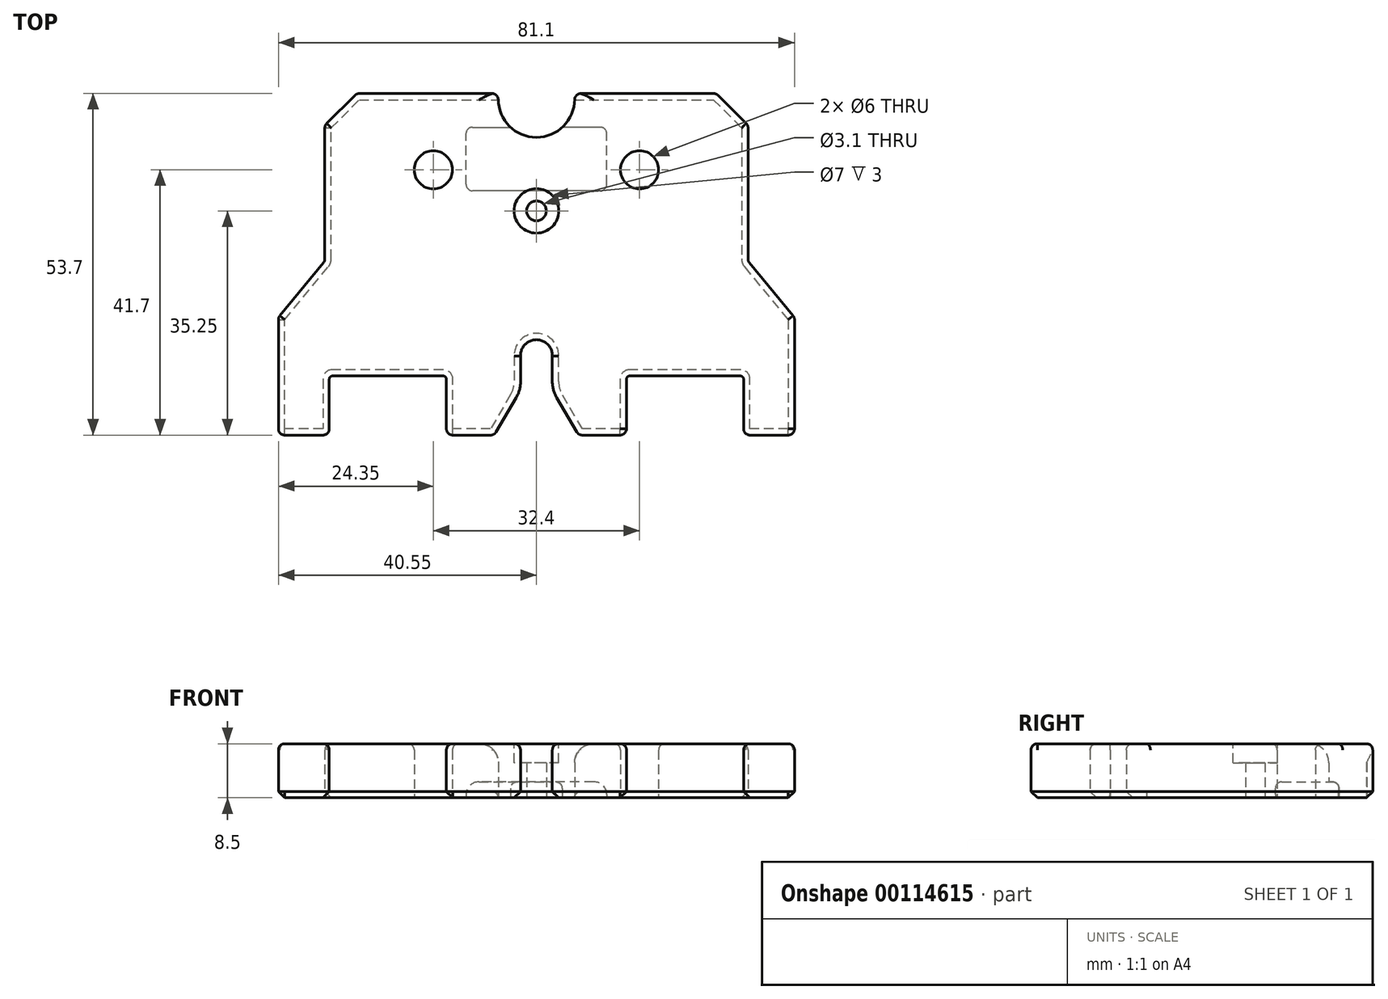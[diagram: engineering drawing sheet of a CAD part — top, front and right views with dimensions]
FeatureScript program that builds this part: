
annotation { "Feature Type Name" : "Feature", "Feature Type Description" : "" }
export const myFeature = defineFeature(function(context is Context, id is Id, definition is map)
    precondition{}
    {
        {
            var Q0;
            Q0=qCreatedBy(makeId("Top.planeOp"),FACE);
            var sketch = newSketch(context, id + "F0", { "sketchPlane" : qUnion([Q0])});
            skLineSegment(sketch, "E0.bottom", {"start": v(7.21, 0) * mm, "end": v(13.15, 0) * mm});
            skLineSegment(sketch, "E0.top", {"start": v(7, 53.7) * mm, "end": v(27.84, 53.7) * mm});
            skLineSegment(sketch, "E0.right", {"start": v(40.55, 1) * mm, "end": v(40.55, 18.14) * mm});
            skCircle(sketch, "E1", {"center": v(40.55, 0) * mm, "radius": 8 * mm, "construction": true});
            skLineSegment(sketch, "E2", {"start": v(32.55, 1) * mm, "end": v(32.55, 8.8) * mm});
            skLineSegment(sketch, "E3", {"start": v(32.05, 9.3) * mm, "end": v(14.65, 9.3) * mm});
            skLineSegment(sketch, "E4", {"start": v(14.15, 8.8) * mm, "end": v(14.15, 1) * mm});
            skCircle(sketch, "E5", {"center": v(14.14, 0) * mm, "radius": 7.5 * mm, "construction": true});
            skArc(sketch, "E6", {"start": v(2.5, 12.43) * mm, "mid": v(1.8, 14.24) * mm, "end": v(0, 15) * mm});
            skLineSegment(sketch, "E7", {"start": v(2.5, 12.43) * mm, "end": v(2.5, 8.4) * mm});
            skLineSegment(sketch, "E8.trimOffspring", {"start": v(33.55, 0) * mm, "end": v(39.55, 0) * mm});
            skLineSegment(sketch, "E9.trimOffspring", {"start": v(0, 15) * mm, "end": v(0, 46.8) * mm, "construction": true});
            skPoint(sketch, "E0.left.start.orphan", {"position": v(0, 0) * mm});
            skLineSegment(sketch, "E10", {"start": v(6, 52.8) * mm, "end": v(6, 52.7) * mm});
            skArc(sketch, "E11.trimOffspring", {"start": v(0, 46.8) * mm, "mid": v(4.24, 48.56) * mm, "end": v(6, 52.8) * mm});
            skCircle(sketch, "E12", {"center": v(40.55, 0) * mm, "radius": 18.5 * mm, "construction": true});
            skCircle(sketch, "E13", {"center": v(40.55, 18.5) * mm, "radius": 8.85 * mm, "construction": true});
            skLineSegment(sketch, "E14", {"start": v(28.54, 53.4) * mm, "end": v(32.96, 49) * mm});
            skLineSegment(sketch, "E15", {"start": v(33.25, 48.29) * mm, "end": v(33.25, 27.7) * mm});
            skLineSegment(sketch, "E16", {"start": v(40.32, 18.78) * mm, "end": v(33.48, 27.07) * mm});
            skLineSegment(sketch, "E17", {"start": v(40.55, 27.35) * mm, "end": v(33.25, 27.35) * mm, "construction": true});
            skLineSegment(sketch, "E18", {"start": v(40.55, 27.35) * mm, "end": v(40.55, 18.5) * mm, "construction": true});
            skLineSegment(sketch, "E19", {"start": v(3.2, 5.87) * mm, "end": v(6.35, 0.5) * mm});
            skCircle(sketch, "E20", {"center": v(16.2, 41.7) * mm, "radius": 3 * mm});
            skCircle(sketch, "E21", {"center": v(0, 35.25) * mm, "radius": 1.55 * mm});
            skLineSegment(sketch, "E22", {"start": v(0, 33.7) * mm, "end": v(-9.13, 33.7) * mm, "construction": true});
            skCircle(sketch, "E23", {"center": v(0, 53.7) * mm, "radius": 11.05 * mm, "construction": true});
            skLineSegment(sketch, "E24", {"start": v(11.05, 53.7) * mm, "end": v(11.05, 38.4) * mm, "construction": true});
            skLineSegment(sketch, "E25", {"start": v(11.05, 38.4) * mm, "end": v(-11.05, 38.4) * mm, "construction": true});
            skLineSegment(sketch, "E26", {"start": v(-11.05, 53.54) * mm, "end": v(-11.05, 38.4) * mm, "construction": true});
            skLineSegment(sketch, "E27", {"start": v(0, 36.8) * mm, "end": v(-9.83, 36.8) * mm, "construction": true});
            skCircle(sketch, "E28", {"center": v(11.05, 38.4) * mm, "radius": 10 * mm, "construction": true});
            skLineSegment(sketch, "E29", {"start": v(11.05, 48.4) * mm, "end": v(-11.05, 48.4) * mm, "construction": true});
            skPoint(sketch, "E30.visualSharp", {"position": v(2.5, 7.04) * mm});
            skArc(sketch, "E30.filletArc", {"start": v(2.5, 8.4) * mm, "mid": v(2.67, 7.09) * mm, "end": v(3.2, 5.87) * mm});
            skPoint(sketch, "E31.visualSharp", {"position": v(6.64, 0) * mm});
            skArc(sketch, "E31.filletArc", {"start": v(6.35, 0.5) * mm, "mid": v(6.72, 0.13) * mm, "end": v(7.21, 0) * mm});
            skPoint(sketch, "E32.newPointB", {"position": v(14.15, 0) * mm});
            skArc(sketch, "E32.filletArc", {"start": v(13.15, 0) * mm, "mid": v(13.86, 0.3) * mm, "end": v(14.15, 1) * mm});
            skPoint(sketch, "E33.visualSharp", {"position": v(14.15, 9.3) * mm});
            skArc(sketch, "E33.filletArc", {"start": v(14.65, 9.3) * mm, "mid": v(14.3, 9.15) * mm, "end": v(14.15, 8.8) * mm});
            skPoint(sketch, "E34.visualSharp", {"position": v(32.55, 9.3) * mm});
            skArc(sketch, "E34.filletArc", {"start": v(32.55, 8.8) * mm, "mid": v(32.4, 9.15) * mm, "end": v(32.05, 9.3) * mm});
            skPoint(sketch, "E35.visualSharp", {"position": v(32.55, 0) * mm});
            skArc(sketch, "E35.filletArc", {"start": v(32.55, 1) * mm, "mid": v(32.84, 0.3) * mm, "end": v(33.55, 0) * mm});
            skArc(sketch, "E36.filletArc", {"start": v(39.55, 0) * mm, "mid": v(40.26, 0.3) * mm, "end": v(40.55, 1) * mm});
            skArc(sketch, "E37.filletArc", {"start": v(40.55, 18.14) * mm, "mid": v(40.5, 18.48) * mm, "end": v(40.32, 18.78) * mm});
            skPoint(sketch, "E38.visualSharp", {"position": v(33.25, 27.35) * mm});
            skArc(sketch, "E38.filletArc", {"start": v(33.25, 27.7) * mm, "mid": v(33.3, 27.37) * mm, "end": v(33.48, 27.07) * mm});
            skPoint(sketch, "E39.visualSharp", {"position": v(33.25, 48.7) * mm});
            skArc(sketch, "E39.filletArc", {"start": v(33.25, 48.29) * mm, "mid": v(33.17, 48.67) * mm, "end": v(32.96, 49) * mm});
            skPoint(sketch, "E40.visualSharp", {"position": v(28.25, 53.7) * mm});
            skArc(sketch, "E40.filletArc", {"start": v(28.54, 53.4) * mm, "mid": v(28.22, 53.62) * mm, "end": v(27.84, 53.7) * mm});
            skPoint(sketch, "E41.visualSharp", {"position": v(6, 53.7) * mm});
            skArc(sketch, "E41.filletArc", {"start": v(7, 53.7) * mm, "mid": v(6.3, 53.4) * mm, "end": v(6, 52.7) * mm});
            skArc(sketch, "E42.MirrorCS", {"start": v(0, 46.8) * mm, "mid": v(-4.24, 48.56) * mm, "end": v(-6, 52.8) * mm});
            skArc(sketch, "E43.MirrorCS", {"start": v(-7, 53.7) * mm, "mid": v(-6.3, 53.4) * mm, "end": v(-6, 52.7) * mm});
            skLineSegment(sketch, "E44.MirrorCS", {"start": v(-6, 52.8) * mm, "end": v(-6, 52.7) * mm});
            skLineSegment(sketch, "E45.MirrorCS", {"start": v(-7, 53.7) * mm, "end": v(-27.84, 53.7) * mm});
            skArc(sketch, "E46.MirrorCS", {"start": v(-28.54, 53.4) * mm, "mid": v(-28.22, 53.62) * mm, "end": v(-27.84, 53.7) * mm});
            skLineSegment(sketch, "E47.MirrorCS", {"start": v(-28.54, 53.4) * mm, "end": v(-32.96, 49) * mm});
            skArc(sketch, "E48.MirrorCS", {"start": v(-33.25, 48.29) * mm, "mid": v(-33.17, 48.67) * mm, "end": v(-32.96, 49) * mm});
            skLineSegment(sketch, "E49.MirrorCS", {"start": v(-33.25, 48.29) * mm, "end": v(-33.25, 27.7) * mm});
            skArc(sketch, "E50.MirrorCS", {"start": v(-33.25, 27.7) * mm, "mid": v(-33.3, 27.37) * mm, "end": v(-33.48, 27.07) * mm});
            skLineSegment(sketch, "E51.MirrorCS", {"start": v(-40.32, 18.78) * mm, "end": v(-33.48, 27.07) * mm});
            skArc(sketch, "E52.MirrorCS", {"start": v(-40.55, 18.14) * mm, "mid": v(-40.5, 18.48) * mm, "end": v(-40.32, 18.78) * mm});
            skLineSegment(sketch, "E53.MirrorCS", {"start": v(-40.55, 1) * mm, "end": v(-40.55, 18.14) * mm});
            skArc(sketch, "E54.MirrorCS", {"start": v(-39.55, 0) * mm, "mid": v(-40.26, 0.3) * mm, "end": v(-40.55, 1) * mm});
            skLineSegment(sketch, "E55.MirrorCS", {"start": v(-33.55, 0) * mm, "end": v(-39.55, 0) * mm});
            skArc(sketch, "E56.MirrorCS", {"start": v(-32.55, 1) * mm, "mid": v(-32.84, 0.3) * mm, "end": v(-33.55, 0) * mm});
            skLineSegment(sketch, "E57.MirrorCS", {"start": v(-32.55, 1) * mm, "end": v(-32.55, 8.8) * mm});
            skArc(sketch, "E58.MirrorCS", {"start": v(-32.55, 8.8) * mm, "mid": v(-32.4, 9.15) * mm, "end": v(-32.05, 9.3) * mm});
            skLineSegment(sketch, "E59.MirrorCS", {"start": v(-32.05, 9.3) * mm, "end": v(-14.65, 9.3) * mm});
            skArc(sketch, "E60.MirrorCS", {"start": v(-14.65, 9.3) * mm, "mid": v(-14.3, 9.15) * mm, "end": v(-14.15, 8.8) * mm});
            skLineSegment(sketch, "E61.MirrorCS", {"start": v(-14.15, 8.8) * mm, "end": v(-14.15, 1) * mm});
            skArc(sketch, "E62.MirrorCS", {"start": v(-13.15, 0) * mm, "mid": v(-13.86, 0.3) * mm, "end": v(-14.15, 1) * mm});
            skLineSegment(sketch, "E63.MirrorCS", {"start": v(-7.21, 0) * mm, "end": v(-13.15, 0) * mm});
            skArc(sketch, "E64.MirrorCS", {"start": v(-6.35, 0.5) * mm, "mid": v(-6.72, 0.13) * mm, "end": v(-7.21, 0) * mm});
            skLineSegment(sketch, "E65.MirrorCS", {"start": v(-3.2, 5.87) * mm, "end": v(-6.35, 0.5) * mm});
            skArc(sketch, "E66.MirrorCS", {"start": v(-2.5, 8.4) * mm, "mid": v(-2.67, 7.09) * mm, "end": v(-3.2, 5.87) * mm});
            skLineSegment(sketch, "E67.MirrorCS", {"start": v(-2.5, 12.43) * mm, "end": v(-2.5, 8.4) * mm});
            skArc(sketch, "E68.MirrorCS", {"start": v(-2.5, 12.43) * mm, "mid": v(-1.8, 14.24) * mm, "end": v(0, 15) * mm});
            skCircle(sketch, "E69.MirrorC", {"center": v(-16.2, 41.7) * mm, "radius": 3 * mm});
            skSolve(sketch);
        }
        {
            var Q0;
            Q0=makeQuery(id+"F0.imprint","IMPRINT",FACE,{"disambiguationData":[TD([[makeQuery(id+"F0.imprint","IMPRINT",EDGE,{"derivedFrom":sQuery(id+"F0.wireOp",EDGE,"E0.bottom")}),1.0]])]});
            extrude(context, id + "F1", {"entities" : qUnion([Q0]), "depth" : 8.5 * mm});
        }
        {
            var Q0;
            Q0=makeQuery(id+"F1.opExtrude","CAP_FACE",FACE,{"disambiguationData":[OSD([sQuery(id+"F0.wireOp",EDGE,"E0.bottom"),sQuery(id+"F0.wireOp",EDGE,"E0.top"),sQuery(id+"F0.wireOp",EDGE,"E0.right"),sQuery(id+"F0.wireOp",EDGE,"E2"),sQuery(id+"F0.wireOp",EDGE,"E3"),sQuery(id+"F0.wireOp",EDGE,"E4"),sQuery(id+"F0.wireOp",EDGE,"E6"),sQuery(id+"F0.wireOp",EDGE,"E7"),sQuery(id+"F0.wireOp",EDGE,"E8.trimOffspring"),sQuery(id+"F0.wireOp",EDGE,"E10"),sQuery(id+"F0.wireOp",EDGE,"E11.trimOffspring"),sQuery(id+"F0.wireOp",EDGE,"E14"),sQuery(id+"F0.wireOp",EDGE,"E15"),sQuery(id+"F0.wireOp",EDGE,"E16"),sQuery(id+"F0.wireOp",EDGE,"E19"),sQuery(id+"F0.wireOp",EDGE,"E20"),sQuery(id+"F0.wireOp",EDGE,"E21"),sQuery(id+"F0.wireOp",EDGE,"E30.filletArc"),sQuery(id+"F0.wireOp",EDGE,"E31.filletArc"),sQuery(id+"F0.wireOp",EDGE,"E32.filletArc"),sQuery(id+"F0.wireOp",EDGE,"E33.filletArc"),sQuery(id+"F0.wireOp",EDGE,"E34.filletArc"),sQuery(id+"F0.wireOp",EDGE,"E35.filletArc"),sQuery(id+"F0.wireOp",EDGE,"E36.filletArc"),sQuery(id+"F0.wireOp",EDGE,"E37.filletArc"),sQuery(id+"F0.wireOp",EDGE,"E38.filletArc"),sQuery(id+"F0.wireOp",EDGE,"E39.filletArc"),sQuery(id+"F0.wireOp",EDGE,"E40.filletArc"),sQuery(id+"F0.wireOp",EDGE,"E41.filletArc"),sQuery(id+"F0.wireOp",EDGE,"E42.MirrorCS"),sQuery(id+"F0.wireOp",EDGE,"E43.MirrorCS"),sQuery(id+"F0.wireOp",EDGE,"E44.MirrorCS"),sQuery(id+"F0.wireOp",EDGE,"E45.MirrorCS"),sQuery(id+"F0.wireOp",EDGE,"E46.MirrorCS"),sQuery(id+"F0.wireOp",EDGE,"E47.MirrorCS"),sQuery(id+"F0.wireOp",EDGE,"E48.MirrorCS"),sQuery(id+"F0.wireOp",EDGE,"E49.MirrorCS"),sQuery(id+"F0.wireOp",EDGE,"E50.MirrorCS"),sQuery(id+"F0.wireOp",EDGE,"E51.MirrorCS"),sQuery(id+"F0.wireOp",EDGE,"E52.MirrorCS"),sQuery(id+"F0.wireOp",EDGE,"E53.MirrorCS"),sQuery(id+"F0.wireOp",EDGE,"E54.MirrorCS"),sQuery(id+"F0.wireOp",EDGE,"E55.MirrorCS"),sQuery(id+"F0.wireOp",EDGE,"E56.MirrorCS"),sQuery(id+"F0.wireOp",EDGE,"E57.MirrorCS"),sQuery(id+"F0.wireOp",EDGE,"E58.MirrorCS"),sQuery(id+"F0.wireOp",EDGE,"E59.MirrorCS"),sQuery(id+"F0.wireOp",EDGE,"E60.MirrorCS"),sQuery(id+"F0.wireOp",EDGE,"E61.MirrorCS"),sQuery(id+"F0.wireOp",EDGE,"E62.MirrorCS"),sQuery(id+"F0.wireOp",EDGE,"E63.MirrorCS"),sQuery(id+"F0.wireOp",EDGE,"E64.MirrorCS"),sQuery(id+"F0.wireOp",EDGE,"E65.MirrorCS"),sQuery(id+"F0.wireOp",EDGE,"E66.MirrorCS"),sQuery(id+"F0.wireOp",EDGE,"E67.MirrorCS"),sQuery(id+"F0.wireOp",EDGE,"E68.MirrorCS"),sQuery(id+"F0.wireOp",EDGE,"E69.MirrorC")])],"isStart":false});
            var sketch = newSketch(context, id + "F2", { "sketchPlane" : qUnion([Q0])});
            skCircle(sketch, "E70", {"center": v(0, 35.25) * mm, "radius": 3.5 * mm});
            skSolve(sketch);
        }
        {
            var Q0;
            Q0=makeQuery(id+"F2.imprint","IMPRINT",FACE,{"disambiguationData":[TD([[makeQuery(id+"F2.imprint","IMPRINT",EDGE,{"derivedFrom":sQuery(id+"F2.wireOp",EDGE,"E70")}),1.0]])]});
            extrude(context, id + "F3", {"entities" : qUnion([Q0]), "operationType" : NewBodyOperationType.REMOVE, "oppositeDirection" : true, "depth" : 3 * mm});
        }
        {
            var Q0;
            Q0=makeQuery(id+"F0.imprint","IMPRINT",FACE,{"disambiguationData":[TD([[makeQuery(id+"F0.imprint","IMPRINT",EDGE,{"derivedFrom":sQuery(id+"F0.wireOp",EDGE,"E0.bottom")}),1.0]])]});
            var sketch = newSketch(context, id + "F4", { "sketchPlane" : qUnion([Q0])});
            skLineSegment(sketch, "E71", {"start": v(0, 54.27) * mm, "end": v(0, 38.4) * mm, "construction": true});
            skLineSegment(sketch, "E72", {"start": v(0, 38.4) * mm, "end": v(11.05, 38.4) * mm});
            skLineSegment(sketch, "E73", {"start": v(11.05, 38.4) * mm, "end": v(11.05, 48.4) * mm});
            skLineSegment(sketch, "E74", {"start": v(11.05, 48.4) * mm, "end": v(0, 48.4) * mm});
            skLineSegment(sketch, "E75.MirrorCS", {"start": v(0, 38.4) * mm, "end": v(-11.05, 38.4) * mm});
            skLineSegment(sketch, "E76.MirrorCS", {"start": v(-11.05, 38.4) * mm, "end": v(-11.05, 48.4) * mm});
            skLineSegment(sketch, "E77.MirrorCS", {"start": v(-11.05, 48.4) * mm, "end": v(0, 48.4) * mm});
            skSolve(sketch);
        }
        {
            var Q0;
            Q0=makeQuery(id+"F4.imprint","IMPRINT",FACE,{"disambiguationData":[TD([[makeQuery(id+"F4.imprint","IMPRINT",EDGE,{"derivedFrom":sQuery(id+"F4.wireOp",EDGE,"E72")}),1.0]])]});
            extrude(context, id + "F5", {"entities" : qUnion([Q0]), "operationType" : NewBodyOperationType.REMOVE, "depth" : 2.5 * mm});
        }
        {
            var Q0;
            Q0=makeQuery(id+"F5.boolean.opBoolean","COPY",EDGE,{"derivedFrom":makeQuery(id+"F5.opExtrude","CAP_EDGE",EDGE,{"disambiguationData":[OSD([sQuery(id+"F4.wireOp",EDGE,"E73")])],"isStart":false})});
            var Q1;
            Q1=makeQuery(id+"F5.boolean.opBoolean","COPY",EDGE,{"derivedFrom":makeQuery(id+"F5.opExtrude","CAP_EDGE",EDGE,{"disambiguationData":[OSD([sQuery(id+"F4.wireOp",EDGE,"E76.MirrorCS")])],"isStart":false})});
            fillet(context, id + "F6", {"entities" : qUnion([Q0, Q1]), "radius" : 2 * mm, "tangentPropagation" : true, "allowEdgeOverflow" : false});
        }
        {
            var Q0;
            Q0=makeQuery(id+"F5.boolean.opBoolean","COPY",EDGE,{"derivedFrom":makeQuery(id+"F5.opExtrude","CAP_EDGE",EDGE,{"disambiguationData":[OSD([sQuery(id+"F4.wireOp",EDGE,"E77.MirrorCS")])],"isStart":false})});
            var Q1;
            Q1=makeQuery(id+"F5.boolean.opBoolean","COPY",EDGE,{"derivedFrom":makeQuery(id+"F5.opExtrude","CAP_EDGE",EDGE,{"disambiguationData":[OSD([sQuery(id+"F4.wireOp",EDGE,"E74")])],"isStart":false})});
            var Q2;
            Q2=makeQuery(id+"F5.boolean.opBoolean","COPY",EDGE,{"derivedFrom":makeQuery(id+"F5.opExtrude","CAP_EDGE",EDGE,{"disambiguationData":[OSD([sQuery(id+"F4.wireOp",EDGE,"E72"),sQuery(id+"F4.wireOp",EDGE,"E75.MirrorCS")])],"isStart":false})});
            fillet(context, id + "F7", {"entities" : qUnion([Q0, Q1, Q2]), "radius" : 1 * mm, "tangentPropagation" : true, "allowEdgeOverflow" : false});
        }
        {
            var Q0;
            Q0=makeQuery(id+"F1.opExtrude","CAP_EDGE",EDGE,{"disambiguationData":[OSD([sQuery(id+"F0.wireOp",EDGE,"E0.top")])],"isStart":false});
            var Q1;
            Q1=makeQuery(id+"F1.opExtrude","CAP_EDGE",EDGE,{"disambiguationData":[OSD([sQuery(id+"F0.wireOp",EDGE,"E41.filletArc")])],"isStart":false});
            var Q2;
            Q2=makeQuery(id+"F1.opExtrude","CAP_EDGE",EDGE,{"disambiguationData":[OSD([sQuery(id+"F0.wireOp",EDGE,"E43.MirrorCS")])],"isStart":false});
            var Q3;
            Q3=makeQuery(id+"F1.opExtrude","CAP_EDGE",EDGE,{"disambiguationData":[OSD([sQuery(id+"F0.wireOp",EDGE,"E69.MirrorC")])],"isStart":false});
            var Q4;
            Q4=makeQuery(id+"F1.opExtrude","CAP_EDGE",EDGE,{"disambiguationData":[OSD([sQuery(id+"F0.wireOp",EDGE,"E20")])],"isStart":false});
            fillet(context, id + "F8", {"entities" : qUnion([Q0, Q1, Q2, Q3, Q4]), "radius" : 1 * mm, "tangentPropagation" : true, "allowEdgeOverflow" : false});
        }
        {
            var Q0;
            Q0=makeQuery(id+"F1.opExtrude","CAP_EDGE",EDGE,{"disambiguationData":[OSD([sQuery(id+"F0.wireOp",EDGE,"E11.trimOffspring"),sQuery(id+"F0.wireOp",EDGE,"E42.MirrorCS")])],"isStart":false});
            fillet(context, id + "F9", {"entities" : qUnion([Q0]), "radius" : 3 * mm, "tangentPropagation" : true, "allowEdgeOverflow" : false});
        }
        {
            var Q0;
            Q0=makeQuery(id+"F1.opExtrude","CAP_EDGE",EDGE,{"disambiguationData":[OSD([sQuery(id+"F0.wireOp",EDGE,"E65.MirrorCS")])],"isStart":true});
            var Q1;
            Q1=makeQuery(id+"F1.opExtrude","CAP_EDGE",EDGE,{"disambiguationData":[OSD([sQuery(id+"F0.wireOp",EDGE,"E19")])],"isStart":true});
            chamfer(context, id + "F10", {"entities" : qUnion([Q0, Q1]), "width" : 1 * mm, "tangentPropagation" : true});
        }
    });
